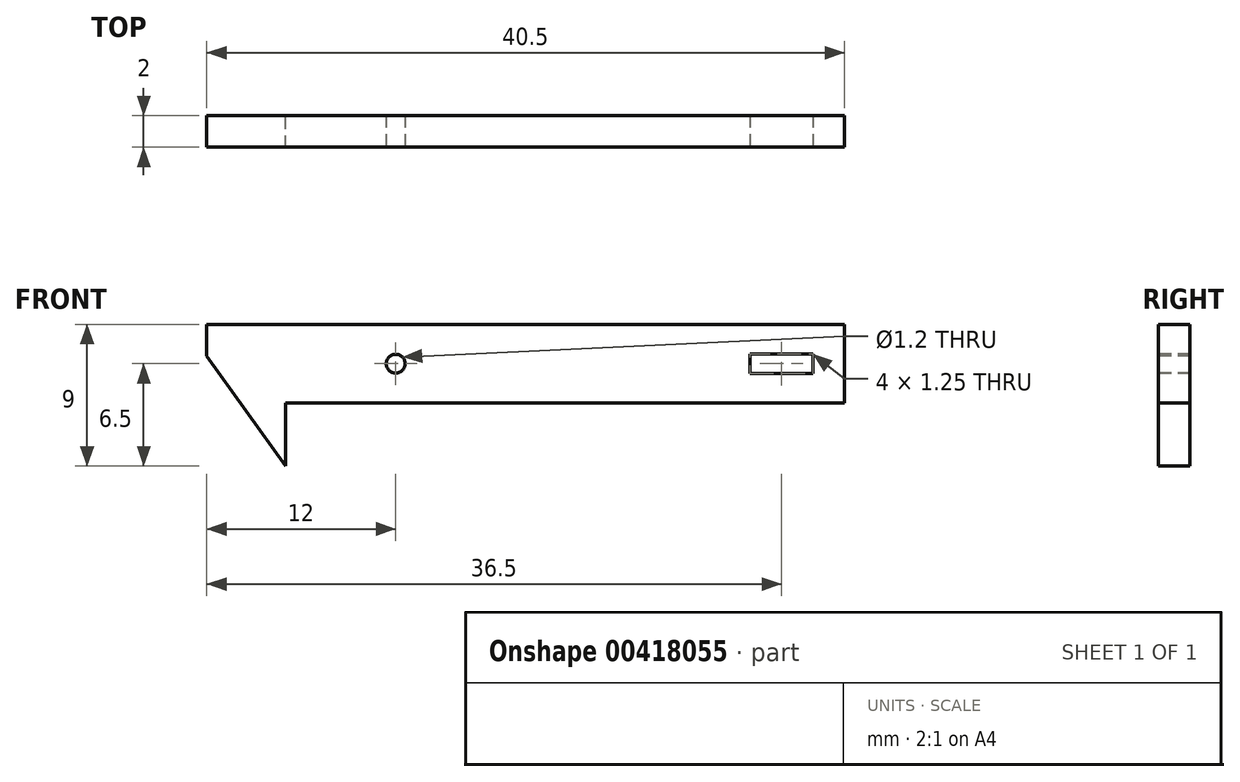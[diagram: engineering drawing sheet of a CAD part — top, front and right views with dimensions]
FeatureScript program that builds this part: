
annotation { "Feature Type Name" : "Feature", "Feature Type Description" : "" }
export const myFeature = defineFeature(function(context is Context, id is Id, definition is map)
    precondition{}
    {
        {
            var Q0;
            Q0=qCreatedBy(makeId("Front.planeOp"),FACE);
            var sketch = newSketch(context, id + "F0", { "sketchPlane" : qUnion([Q0])});
            skLineSegment(sketch, "E0.bottom", {"start": v(0, 0) * mm, "end": v(-40.5, 0) * mm});
            skLineSegment(sketch, "E0.top", {"start": v(0, 5) * mm, "end": v(-40.5, 5) * mm});
            skLineSegment(sketch, "E0.left", {"start": v(0, 0) * mm, "end": v(0, 5) * mm});
            skLineSegment(sketch, "E0.right", {"start": v(-40.5, 0) * mm, "end": v(-40.5, 5) * mm});
            skSolve(sketch);
        }
        {
            var Q0;
            Q0=makeQuery(id+"F0.imprint","IMPRINT",FACE,{"disambiguationData":[TD([[makeQuery(id+"F0.imprint","IMPRINT",EDGE,{"derivedFrom":sQuery(id+"F0.wireOp",EDGE,"E0.bottom")}),-1.0]])]});
            extrude(context, id + "F1", {"entities" : qUnion([Q0]), "depth" : 2 * mm});
        }
        {
            var Q0;
            Q0=qCreatedBy(makeId("Front.planeOp"),FACE);
            var sketch = newSketch(context, id + "F2", { "sketchPlane" : qUnion([Q0])});
            skLineSegment(sketch, "E1.bottom", {"start": v(-40.5, 0) * mm, "end": v(-35.5, 0) * mm});
            skLineSegment(sketch, "E1.top", {"start": v(-40.5, -4) * mm, "end": v(-35.5, -4) * mm});
            skLineSegment(sketch, "E1.left", {"start": v(-40.5, 0) * mm, "end": v(-40.5, -4) * mm});
            skLineSegment(sketch, "E1.right", {"start": v(-35.5, 0) * mm, "end": v(-35.5, -4) * mm});
            skSolve(sketch);
        }
        {
            var Q0;
            Q0=qSketchRegion(id+"F2",true);
            extrude(context, id + "F3", {"entities" : qUnion([Q0]), "operationType" : NewBodyOperationType.ADD, "depth" : 2 * mm});
        }
        {
            var Q0;
            Q0=makeQuery(id+"F3.opExtrude","SWEPT_EDGE",EDGE,{"disambiguationData":[OSD([sQuery(id+"F2.wireOp",EDGE,"E1.top"),sQuery(id+"F2.wireOp",EDGE,"E1.left")])]});
            chamfer(context, id + "F4", {"entities" : qUnion([Q0]), "chamferType" : ChamferType.TWO_OFFSETS, "width1" : 5 * mm, "oppositeDirection" : false, "width2" : 7 * mm, "tangentPropagation" : true});
        }
        {
            var Q0;
            Q0=makeQuery(id+"F3.boolean.opBoolean","MERGE",FACE,{"derivedFrom":[makeQuery(id+"F1.opExtrude","CAP_FACE",FACE,{"disambiguationData":[OSD([sQuery(id+"F0.wireOp",EDGE,"E0.bottom"),sQuery(id+"F0.wireOp",EDGE,"E0.top"),sQuery(id+"F0.wireOp",EDGE,"E0.left"),sQuery(id+"F0.wireOp",EDGE,"E0.right")])],"isStart":false}),makeQuery(id+"F3.opExtrude","CAP_FACE",FACE,{"disambiguationData":[OSD([sQuery(id+"F2.wireOp",EDGE,"E1.bottom"),sQuery(id+"F2.wireOp",EDGE,"E1.top"),sQuery(id+"F2.wireOp",EDGE,"E1.left"),sQuery(id+"F2.wireOp",EDGE,"E1.right")])],"isStart":false})]});
            var sketch = newSketch(context, id + "F5", { "sketchPlane" : qUnion([Q0])});
            skLineSegment(sketch, "E2.bottom", {"start": v(-2, 1.87) * mm, "end": v(-6, 1.87) * mm});
            skLineSegment(sketch, "E2.top", {"start": v(-2, 3.12) * mm, "end": v(-6, 3.12) * mm});
            skLineSegment(sketch, "E2.left", {"start": v(-2, 1.87) * mm, "end": v(-2, 3.12) * mm});
            skLineSegment(sketch, "E2.right", {"start": v(-6, 1.87) * mm, "end": v(-6, 3.12) * mm});
            skPoint(sketch, "E2.middle", {"position": v(-4, 2.5) * mm});
            skPoint(sketch, "E2.middle.positionSnap0", {"position": v(0, 2.5) * mm});
            skPoint(sketch, "E2.centerSnap0", {"position": v(0, 2.5) * mm});
            skSolve(sketch);
        }
        {
            var Q0;
            Q0=makeQuery(id+"F5.imprint","IMPRINT",FACE,{"disambiguationData":[TD([[makeQuery(id+"F5.imprint","IMPRINT",EDGE,{"derivedFrom":sQuery(id+"F5.wireOp",EDGE,"E2.bottom")}),-1.0]])]});
            extrude(context, id + "F6", {"entities" : qUnion([Q0]), "operationType" : NewBodyOperationType.REMOVE, "oppositeDirection" : true, "depth" : 2 * mm});
        }
        {
            var Q0;
            Q0=makeQuery(id+"F3.boolean.opBoolean","MERGE",FACE,{"derivedFrom":[makeQuery(id+"F1.opExtrude","CAP_FACE",FACE,{"disambiguationData":[OSD([sQuery(id+"F0.wireOp",EDGE,"E0.bottom"),sQuery(id+"F0.wireOp",EDGE,"E0.top"),sQuery(id+"F0.wireOp",EDGE,"E0.left"),sQuery(id+"F0.wireOp",EDGE,"E0.right")])],"isStart":false}),makeQuery(id+"F3.opExtrude","CAP_FACE",FACE,{"disambiguationData":[OSD([sQuery(id+"F2.wireOp",EDGE,"E1.bottom"),sQuery(id+"F2.wireOp",EDGE,"E1.top"),sQuery(id+"F2.wireOp",EDGE,"E1.left"),sQuery(id+"F2.wireOp",EDGE,"E1.right")])],"isStart":false})]});
            var sketch = newSketch(context, id + "F7", { "sketchPlane" : qUnion([Q0])});
            skCircle(sketch, "E3", {"center": v(-28.5, 2.5) * mm, "radius": 0.6 * mm});
            skPoint(sketch, "E3.centerSnap0", {"position": v(-6, 2.5) * mm});
            skSolve(sketch);
        }
        {
            var Q0;
            Q0=makeQuery(id+"F7.imprint","IMPRINT",FACE,{"disambiguationData":[TD([[makeQuery(id+"F7.imprint","IMPRINT",EDGE,{"derivedFrom":sQuery(id+"F7.wireOp",EDGE,"E3")}),1.0]])]});
            extrude(context, id + "F8", {"entities" : qUnion([Q0]), "operationType" : NewBodyOperationType.REMOVE, "oppositeDirection" : true, "depth" : 2 * mm});
        }
    });
